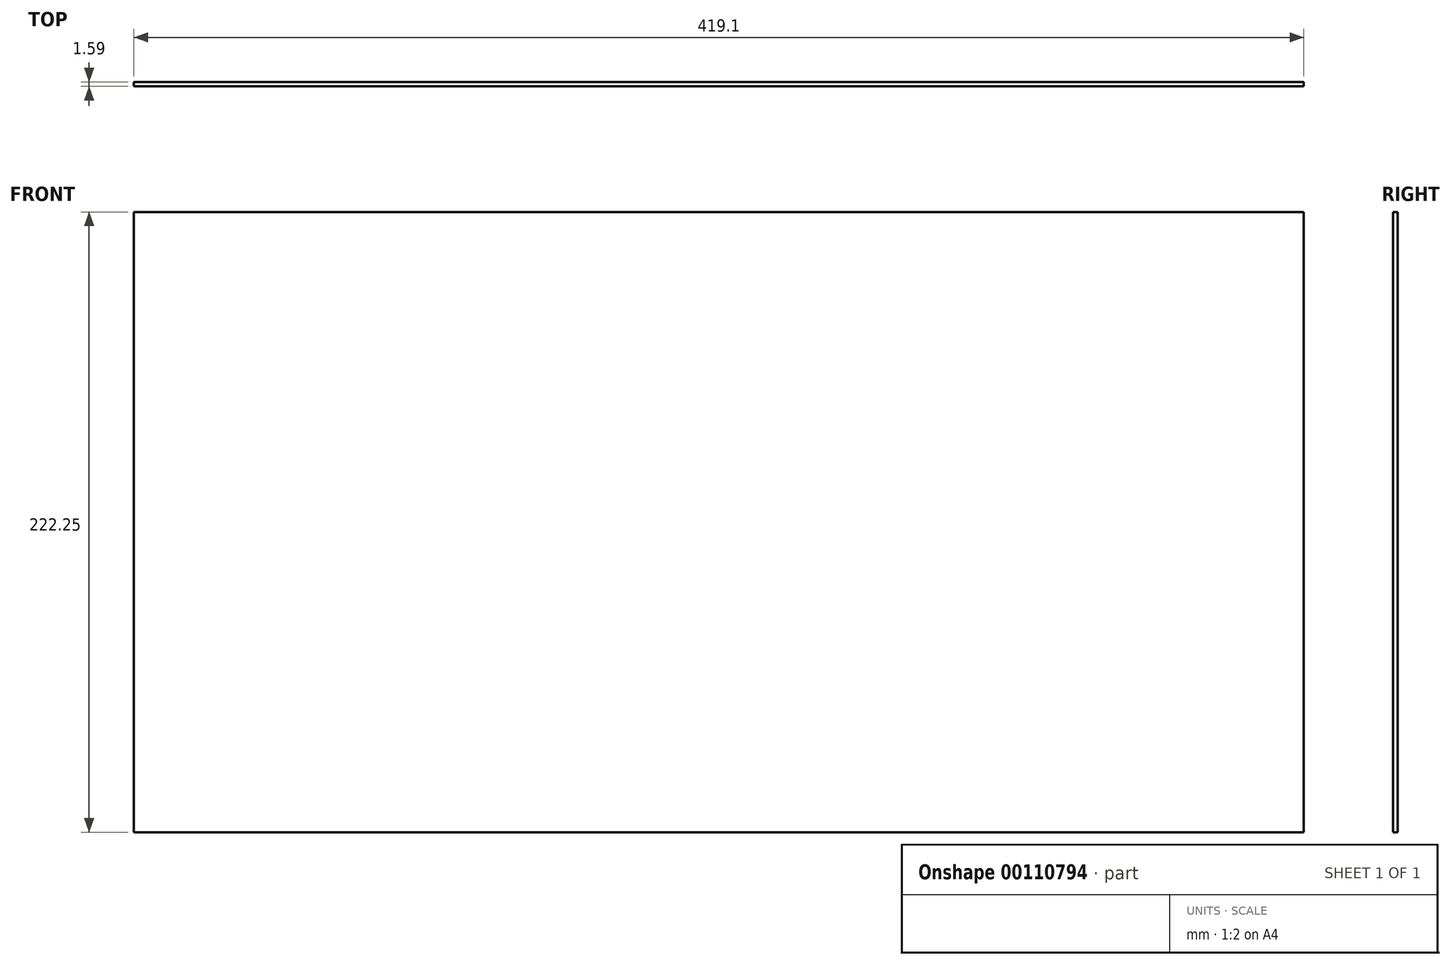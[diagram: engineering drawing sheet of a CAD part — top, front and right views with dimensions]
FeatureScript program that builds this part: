
annotation { "Feature Type Name" : "Feature", "Feature Type Description" : "" }
export const myFeature = defineFeature(function(context is Context, id is Id, definition is map)
    precondition{}
    {
        {
            var Q0;
            Q0=qCreatedBy(makeId("Front.planeOp"),FACE);
            var sketch = newSketch(context, id + "F0", { "sketchPlane" : qUnion([Q0])});
            skLineSegment(sketch, "E0.bottom", {"start": v(-161.04, 182.93) * mm, "end": v(258.06, 182.93) * mm});
            skLineSegment(sketch, "E0.top", {"start": v(-161.04, -39.32) * mm, "end": v(258.06, -39.32) * mm});
            skLineSegment(sketch, "E0.left", {"start": v(-161.04, 182.93) * mm, "end": v(-161.04, -39.32) * mm});
            skLineSegment(sketch, "E0.right", {"start": v(258.06, 182.93) * mm, "end": v(258.06, -39.32) * mm});
            skSolve(sketch);
        }
        {
            var Q0;
            Q0=makeQuery(id+"F0.imprint","IMPRINT",FACE,{"disambiguationData":[TD([[makeQuery(id+"F0.imprint","IMPRINT",EDGE,{"derivedFrom":sQuery(id+"F0.wireOp",EDGE,"E0.bottom")}),-1.0]])]});
            extrude(context, id + "F1", {"entities" : qUnion([Q0]), "depth" : 1.59 * mm});
        }
    });
